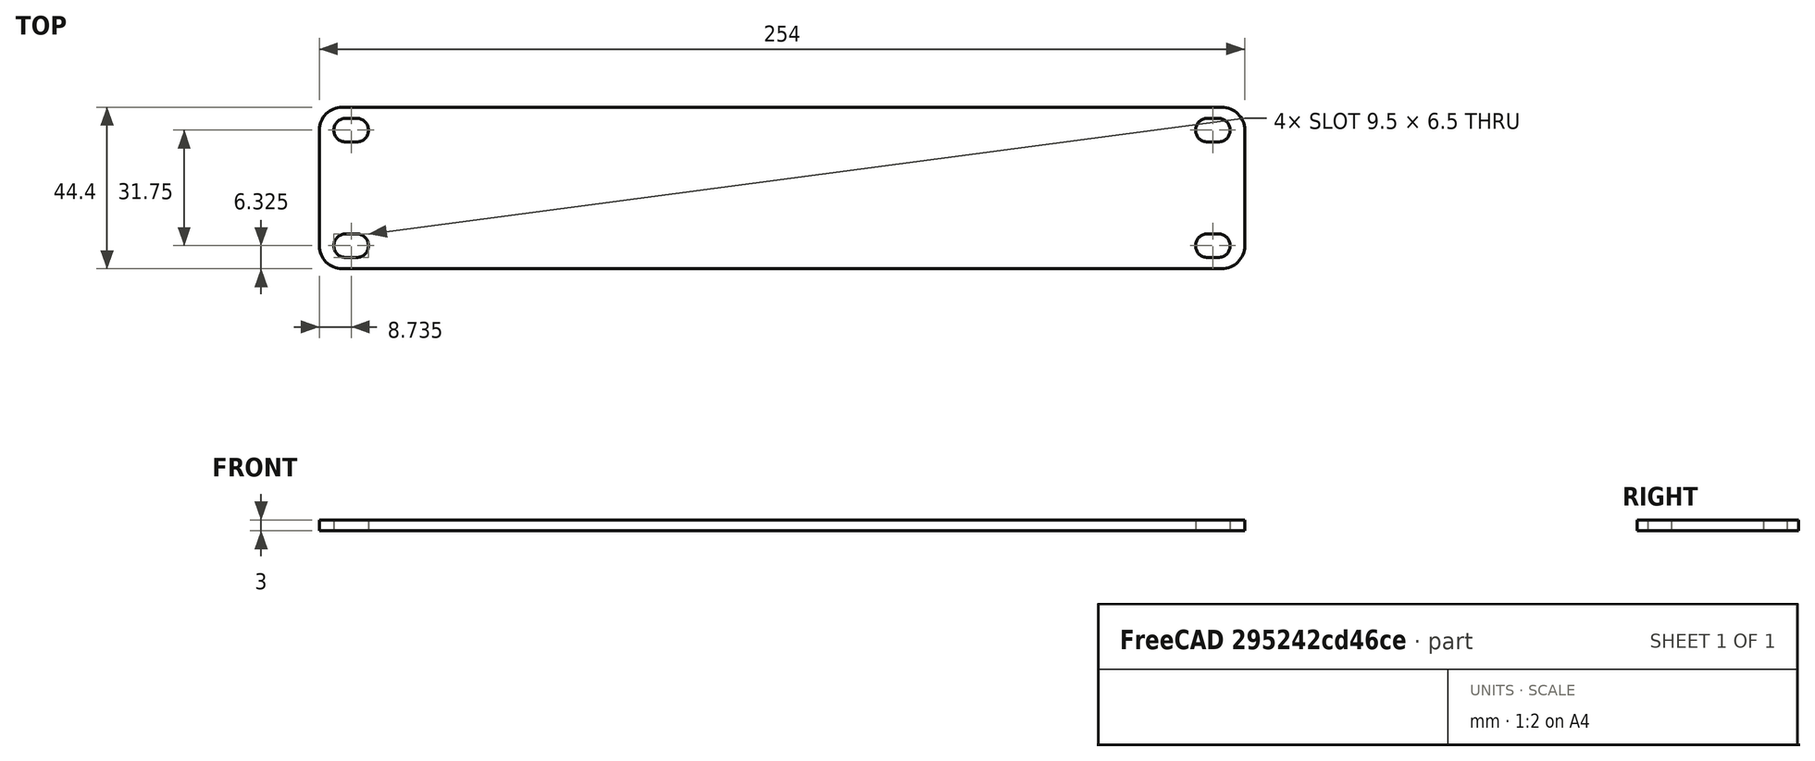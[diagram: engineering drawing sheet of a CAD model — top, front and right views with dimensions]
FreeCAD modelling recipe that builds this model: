
FCSTD DOCUMENT  (FreeCAD 1.1R20260108 (Git shallow))
Label: Generic_BlankPlate
License: All rights reserved
LicenseURL: https://en.wikipedia.org/wiki/All_rights_reserved
objects: App::Point×1, Sketcher::SketchObject×1, PartDesign::Pad×1, PartDesign::Body×1
note: 6 computed .brp shape members not serialized (recipe doc carries the construction recipe); baked Part::Feature solids carry a one-line shape summary decoded from their .brp

FEATURE [App::Point] Origin001
  Role = Origin
FEATURE [Sketcher::SketchObject] Sketch
  ArcFitTolerance = 1e-06
  AttachmentSupport = -> [Origin]
  ExternalTypes = [0]
  FullyConstrained = true
  MakeInternals = false
  MapMode = 5
  sketch-geometry (36):
    g0: LineSegment StartX=6.28 StartY=0 StartZ=0 EndX=247.72 EndY=0 EndZ=0
    g1: LineSegment StartX=254 StartY=6.28 StartZ=0 EndX=254 EndY=38.12 EndZ=0
    g2: LineSegment StartX=247.72 StartY=44.4 StartZ=0 EndX=6.28 EndY=44.4 EndZ=0
    g3: LineSegment StartX=0 StartY=38.12 StartZ=0 EndX=0 EndY=6.28 EndZ=0
    g4: ArcOfCircle CenterX=243.765 CenterY=6.325 CenterZ=0 NormalX=0 NormalY=0 NormalZ=1 AngleXU=0 Radius=3.25 StartAngle=1.5708 EndAngle=4.71239
    g5: ArcOfCircle CenterX=246.765 CenterY=6.325 CenterZ=0 NormalX=0 NormalY=0 NormalZ=1 AngleXU=0 Radius=3.25 StartAngle=4.71239 EndAngle=7.85398
    g6: LineSegment StartX=243.765 StartY=9.575 StartZ=0 EndX=246.765 EndY=9.575 EndZ=0
    g7: LineSegment StartX=243.765 StartY=3.075 StartZ=0 EndX=246.765 EndY=3.075 EndZ=0
    g8: ArcOfCircle CenterX=243.765 CenterY=38.075 CenterZ=0 NormalX=0 NormalY=0 NormalZ=1 AngleXU=0 Radius=3.25 StartAngle=1.5708 EndAngle=4.71239
    g9: ArcOfCircle CenterX=246.765 CenterY=38.075 CenterZ=0 NormalX=0 NormalY=0 NormalZ=1 AngleXU=0 Radius=3.25 StartAngle=4.71239 EndAngle=7.85398
    g10: LineSegment StartX=243.765 StartY=41.325 StartZ=0 EndX=246.765 EndY=41.325 EndZ=0
    g11: LineSegment StartX=243.765 StartY=34.825 StartZ=0 EndX=246.765 EndY=34.825 EndZ=0
    g12: ArcOfCircle CenterX=7.235 CenterY=6.325 CenterZ=0 NormalX=0 NormalY=0 NormalZ=1 AngleXU=0 Radius=3.25 StartAngle=1.5708 EndAngle=4.71239
    g13: ArcOfCircle CenterX=10.235 CenterY=6.325 CenterZ=0 NormalX=0 NormalY=0 NormalZ=1 AngleXU=0 Radius=3.25 StartAngle=4.71239 EndAngle=7.85398
    g14: LineSegment StartX=7.235 StartY=9.575 StartZ=0 EndX=10.235 EndY=9.575 EndZ=0
    g15: LineSegment StartX=7.235 StartY=3.075 StartZ=0 EndX=10.235 EndY=3.075 EndZ=0
    g16: ArcOfCircle CenterX=7.235 CenterY=38.075 CenterZ=0 NormalX=0 NormalY=0 NormalZ=1 AngleXU=0 Radius=3.25 StartAngle=1.5708 EndAngle=4.71239
    g17: ArcOfCircle CenterX=10.235 CenterY=38.075 CenterZ=0 NormalX=0 NormalY=0 NormalZ=1 AngleXU=0 Radius=3.25 StartAngle=4.71239 EndAngle=7.85398
    g18: LineSegment StartX=7.235 StartY=41.325 StartZ=0 EndX=10.235 EndY=41.325 EndZ=0
    g19: LineSegment StartX=7.235 StartY=34.825 StartZ=0 EndX=10.235 EndY=34.825 EndZ=0
    g20: LineSegment [constr] StartX=0 StartY=22.2 StartZ=0 EndX=8.735 EndY=22.2 EndZ=0
    g21: LineSegment [constr] StartX=245.265 StartY=22.2 StartZ=0 EndX=254 EndY=22.2 EndZ=0
    g22: LineSegment [constr] StartX=243.765 StartY=38.075 StartZ=0 EndX=246.765 EndY=38.075 EndZ=0
    g23: LineSegment [constr] StartX=243.765 StartY=6.325 StartZ=0 EndX=246.765 EndY=6.325 EndZ=0
    g24: LineSegment [constr] StartX=245.265 StartY=38.075 StartZ=0 EndX=245.265 EndY=6.325 EndZ=0
    g25: LineSegment [constr] StartX=7.235 StartY=38.075 StartZ=0 EndX=10.235 EndY=38.075 EndZ=0
    g26: LineSegment [constr] StartX=7.235 StartY=6.325 StartZ=0 EndX=10.235 EndY=6.325 EndZ=0
    g27: LineSegment [constr] StartX=8.735 StartY=38.075 StartZ=0 EndX=8.735 EndY=6.325 EndZ=0
    g28: ArcOfCircle CenterX=6.28 CenterY=38.12 CenterZ=0 NormalX=0 NormalY=0 NormalZ=1 AngleXU=0 Radius=6.28 StartAngle=1.5708 EndAngle=3.14159
    g29: GeomPoint [constr] X=0 Y=44.4 Z=0
    g30: ArcOfCircle CenterX=6.28 CenterY=6.28 CenterZ=0 NormalX=0 NormalY=0 NormalZ=1 AngleXU=0 Radius=6.28 StartAngle=3.14159 EndAngle=4.71239
    g31: GeomPoint [constr] X=0 Y=0 Z=0
    g32: ArcOfCircle CenterX=247.72 CenterY=38.12 CenterZ=0 NormalX=0 NormalY=0 NormalZ=1 AngleXU=0 Radius=6.28 StartAngle=0 EndAngle=1.5708
    g33: GeomPoint [constr] X=254 Y=44.4 Z=0
    g34: ArcOfCircle CenterX=247.72 CenterY=6.28 CenterZ=0 NormalX=0 NormalY=0 NormalZ=1 AngleXU=0 Radius=6.28 StartAngle=4.71239 EndAngle=6.28319
    g35: GeomPoint [constr] X=254 Y=0 Z=0
  constraints (83):
    c: Horizontal(g0)
    c: Horizontal(g2)
    c: Vertical(g1)
    c: Vertical(g3)
    c: Distance(g35,g31) = 254
    c: Distance(g31,g29) = 44.4
    c: Coincident(g31,g-1)
    c: Tangent(g4,g6) = 1.5708
    c: Tangent(g4,g7) = -1.5708
    c: Tangent(g5,g6) = 1.5708
    c: Tangent(g5,g7) = -1.5708
    c: Equal(g4,g5)
    c: Distance(g4,g5) = 3
    c: Radius(g4) = 3.25
    c: Horizontal(g6)
    c: Tangent(g8,g10) = 1.5708
    c: Tangent(g8,g11) = -1.5708
    c: Tangent(g9,g10) = 1.5708
    c: Tangent(g9,g11) = -1.5708
    c: Equal(g8,g9)
    c: Distance(g8,g9) = 3
    c: Radius(g8) = 3.25
    c: Horizontal(g10)
    c: DistanceY(g4,g8) = 31.75
    c: Tangent(g12,g14) = 1.5708
    c: Tangent(g12,g15) = -1.5708
    c: Tangent(g13,g14) = 1.5708
    c: Tangent(g13,g15) = -1.5708
    c: Equal(g12,g13)
    c: Distance(g12,g13) = 3
    c: Radius(g12) = 3.25
    c: Horizontal(g14)
    c: Tangent(g16,g18) = 1.5708
    c: Tangent(g16,g19) = -1.5708
    c: Tangent(g17,g18) = 1.5708
    c: Tangent(g17,g19) = -1.5708
    c: Equal(g16,g17)
    c: Distance(g16,g17) = 3
    c: Radius(g16) = 3.25
    c: Horizontal(g18)
    c: Horizontal(g20)
    c: DistanceY(g12,g16) = 31.75
    c: Symmetric(g35,g33,g21)
    c: Horizontal(g21)
    c: Coincident(g22,g8)
    c: Coincident(g22,g9)
    c: Coincident(g23,g4)
    c: Coincident(g23,g5)
    c: Symmetric(g22,g22,g24)
    c: Symmetric(g23,g23,g24)
    c: Vertical(g24)
    c: Symmetric(g24,g24,g21)
    c: Coincident(g25,g16)
    c: Coincident(g25,g17)
    c: Coincident(g26,g12)
    c: Coincident(g26,g13)
    c: Symmetric(g25,g25,g27)
    c: Symmetric(g26,g26,g27)
    c: Vertical(g27)
    c: Symmetric(g27,g27,g20)
    c: Distance(g24,g27) = 236.53
    c: Symmetric(g29,g31,g20)
    c: Equal(g21,g20)
    c: PointOnObject(g29,g2)
    c: PointOnObject(g29,g3)
    c: Tangent(g2,g28) = -1.5708
    c: Tangent(g3,g28) = -1.5708
    c: PointOnObject(g31,g0)
    c: PointOnObject(g31,g3)
    c: Tangent(g0,g30) = -1.5708
    c: Tangent(g3,g30) = -1.5708
    c: PointOnObject(g33,g1)
    c: PointOnObject(g33,g2)
    c: Tangent(g1,g32) = -1.5708
    c: Tangent(g2,g32) = -1.5708
    c: PointOnObject(g35,g0)
    c: PointOnObject(g35,g1)
    c: Tangent(g0,g34) = -1.5708
    c: Tangent(g1,g34) = -1.5708
    c: Equal(g32,g34)
    c: Equal(g34,g28)
    c: Equal(g28,g30)
    c: Radius(g28) = 6.28
FEATURE [PartDesign::Pad] Pad
  Direction = (0,0,1)
  Length = 3
  Length2 = 10
  Profile = -> Sketch
  ReferenceAxis = -> Sketch [N_Axis]
  Refine = true
  SideType = 0
  Suppressed = false
  Type = 0
  Type2 = 0
FEATURE [PartDesign::Body] Body
  AllowCompound = true
  Group = -> [Sketch,Pad]
  Origin = -> Origin
  Tip = -> Pad
